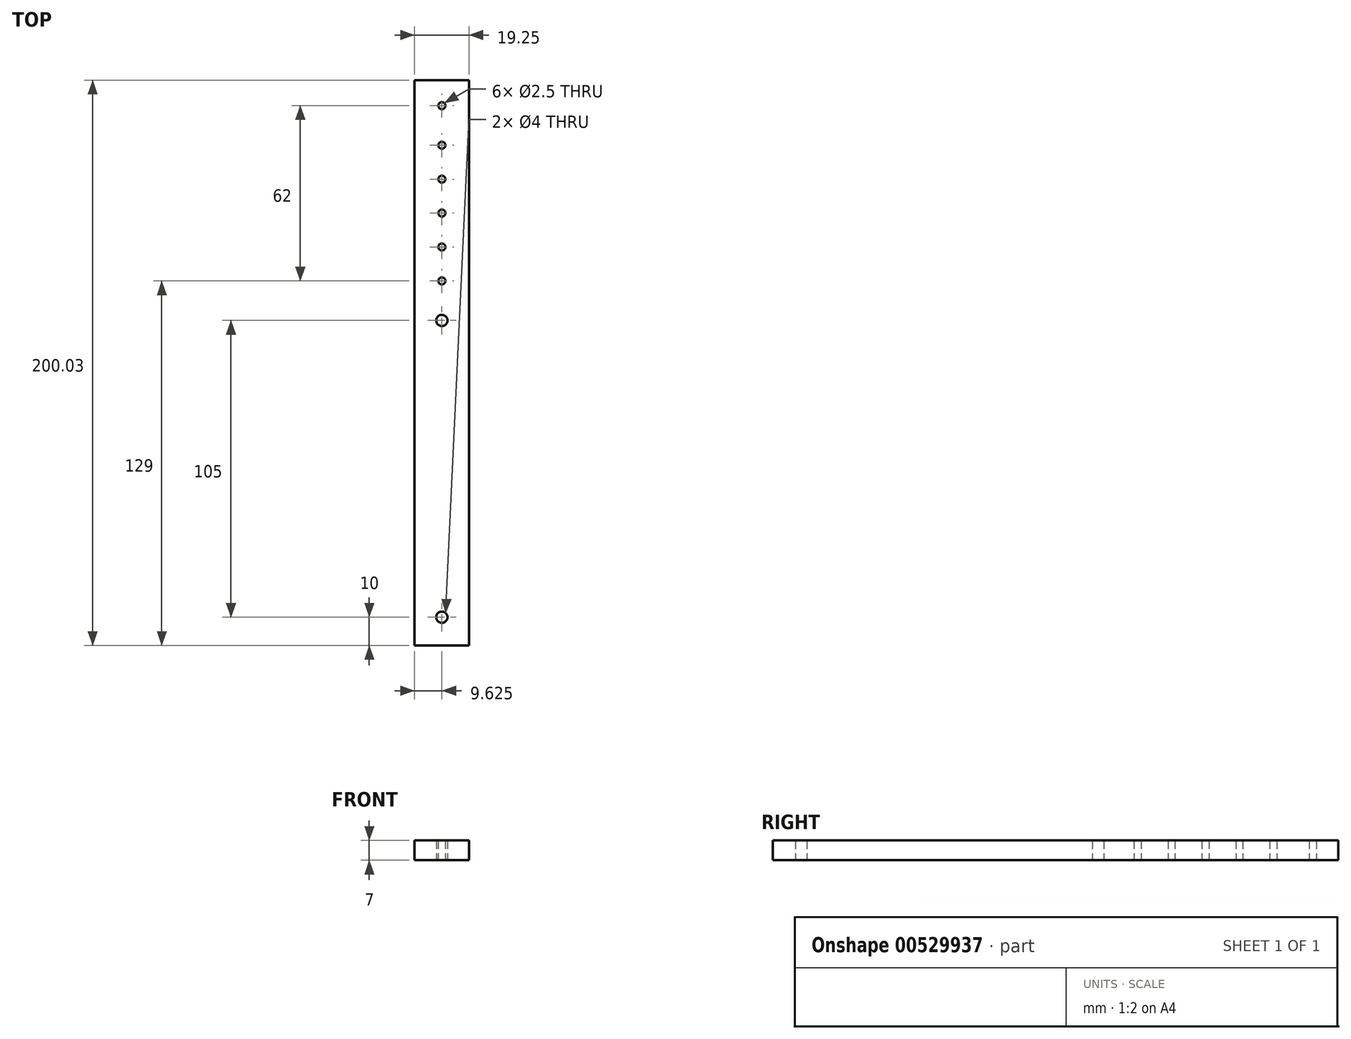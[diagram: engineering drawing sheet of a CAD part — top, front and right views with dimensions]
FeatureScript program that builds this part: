
annotation { "Feature Type Name" : "Feature", "Feature Type Description" : "" }
export const myFeature = defineFeature(function(context is Context, id is Id, definition is map)
    precondition{}
    {
        {
            var Q0;
            Q0=qCreatedBy(makeId("Top.planeOp"),FACE);
            var sketch = newSketch(context, id + "F0", { "sketchPlane" : qUnion([Q0])});
            skLineSegment(sketch, "E0.bottom", {"start": v(0, 0) * mm, "end": v(19.25, 0) * mm});
            skLineSegment(sketch, "E0.top", {"start": v(0, 200.03) * mm, "end": v(19.25, 200.03) * mm});
            skLineSegment(sketch, "E0.left", {"start": v(0, 0) * mm, "end": v(0, 200.03) * mm});
            skLineSegment(sketch, "E0.right", {"start": v(19.25, 0) * mm, "end": v(19.25, 200.03) * mm});
            skLineSegment(sketch, "E1", {"start": v(9.62, -3.29) * mm, "end": v(9.62, 212.6) * mm, "construction": true});
            skCircle(sketch, "E2", {"center": v(9.62, 10) * mm, "radius": 2 * mm});
            skCircle(sketch, "E3", {"center": v(9.62, 115) * mm, "radius": 2 * mm});
            skCircle(sketch, "E4", {"center": v(9.62, 129) * mm, "radius": 1.25 * mm});
            skCircle(sketch, "E5", {"center": v(9.62, 141) * mm, "radius": 1.25 * mm});
            skCircle(sketch, "E6", {"center": v(9.62, 153) * mm, "radius": 1.25 * mm});
            skCircle(sketch, "E7", {"center": v(9.62, 165) * mm, "radius": 1.25 * mm});
            skCircle(sketch, "E8", {"center": v(9.62, 177) * mm, "radius": 1.25 * mm});
            skCircle(sketch, "E9", {"center": v(9.62, 191) * mm, "radius": 1.25 * mm});
            skSolve(sketch);
        }
        {
            var Q0;
            Q0 = qSketchRegion(id + "F0", true);
            extrude(context, id + "F1", {"entities" : qUnion([Q0]), "depth" : 7 * mm, "offsetDistance" : 25 * mm});
        }
    });
